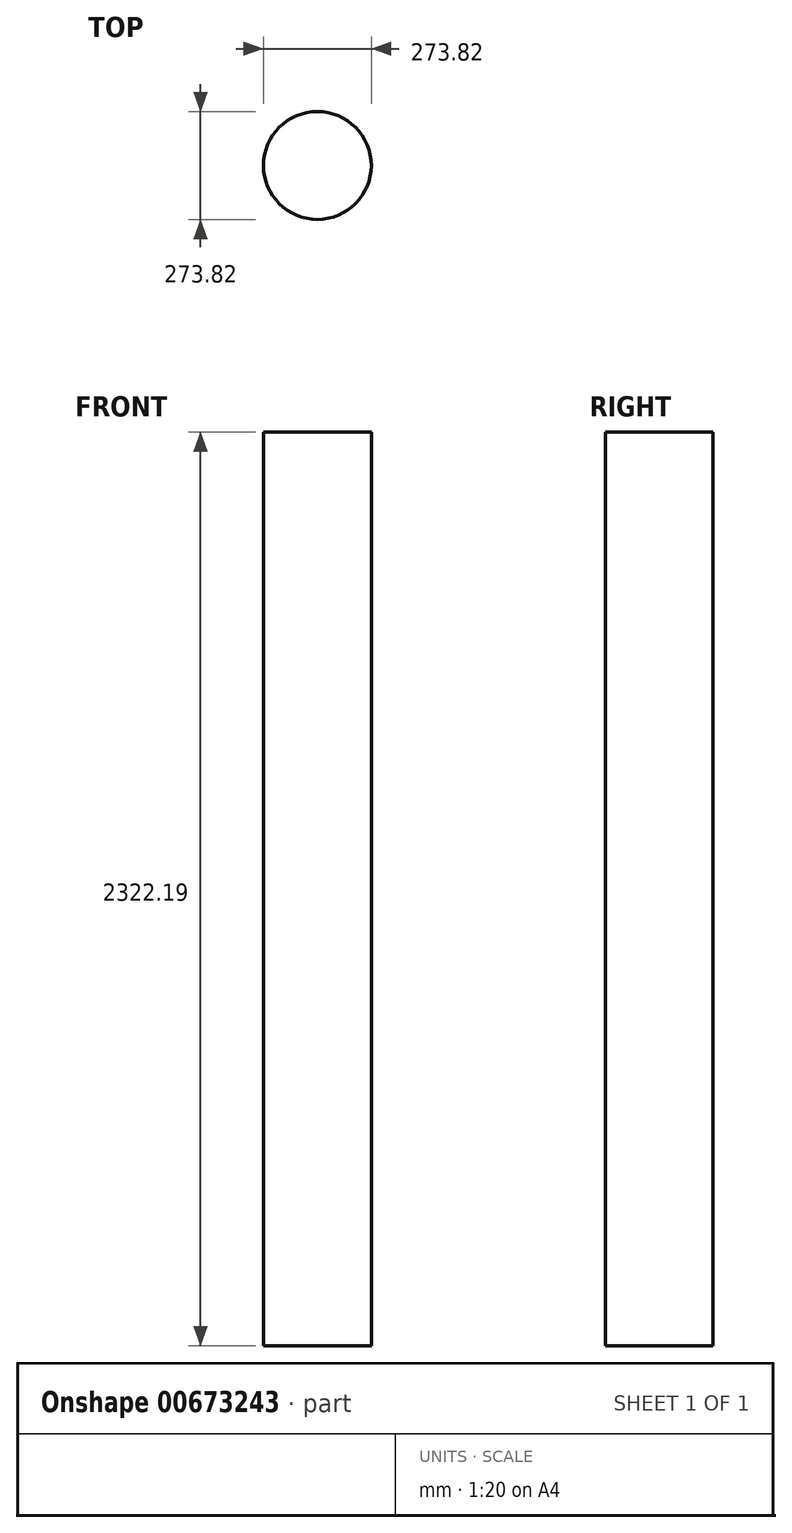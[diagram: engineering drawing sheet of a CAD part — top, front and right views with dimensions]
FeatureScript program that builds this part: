
annotation { "Feature Type Name" : "Feature", "Feature Type Description" : "" }
export const myFeature = defineFeature(function(context is Context, id is Id, definition is map)
    precondition{}
    {
        {
            var Q0;
            Q0=qCreatedBy(makeId("Top.planeOp"),FACE);
            var sketch = newSketch(context, id + "F0", { "sketchPlane" : qUnion([Q0])});
            skCircle(sketch, "E0", {"center": v(0, 0) * mm, "radius": 136.91 * mm});
            skSolve(sketch);
        }
        {
            var Q0;
            Q0=makeQuery(id+"F0.imprint","IMPRINT",FACE,{"disambiguationData":[TD([[makeQuery(id+"F0.imprint","IMPRINT",EDGE,{"derivedFrom":sQuery(id+"F0.wireOp",EDGE,"E0")}),1.0]])]});
            extrude(context, id + "F1", {"entities" : qUnion([Q0]), "depth" : 2322.2 * mm, "offsetDistance" : 25.4 * mm});
        }
    });
